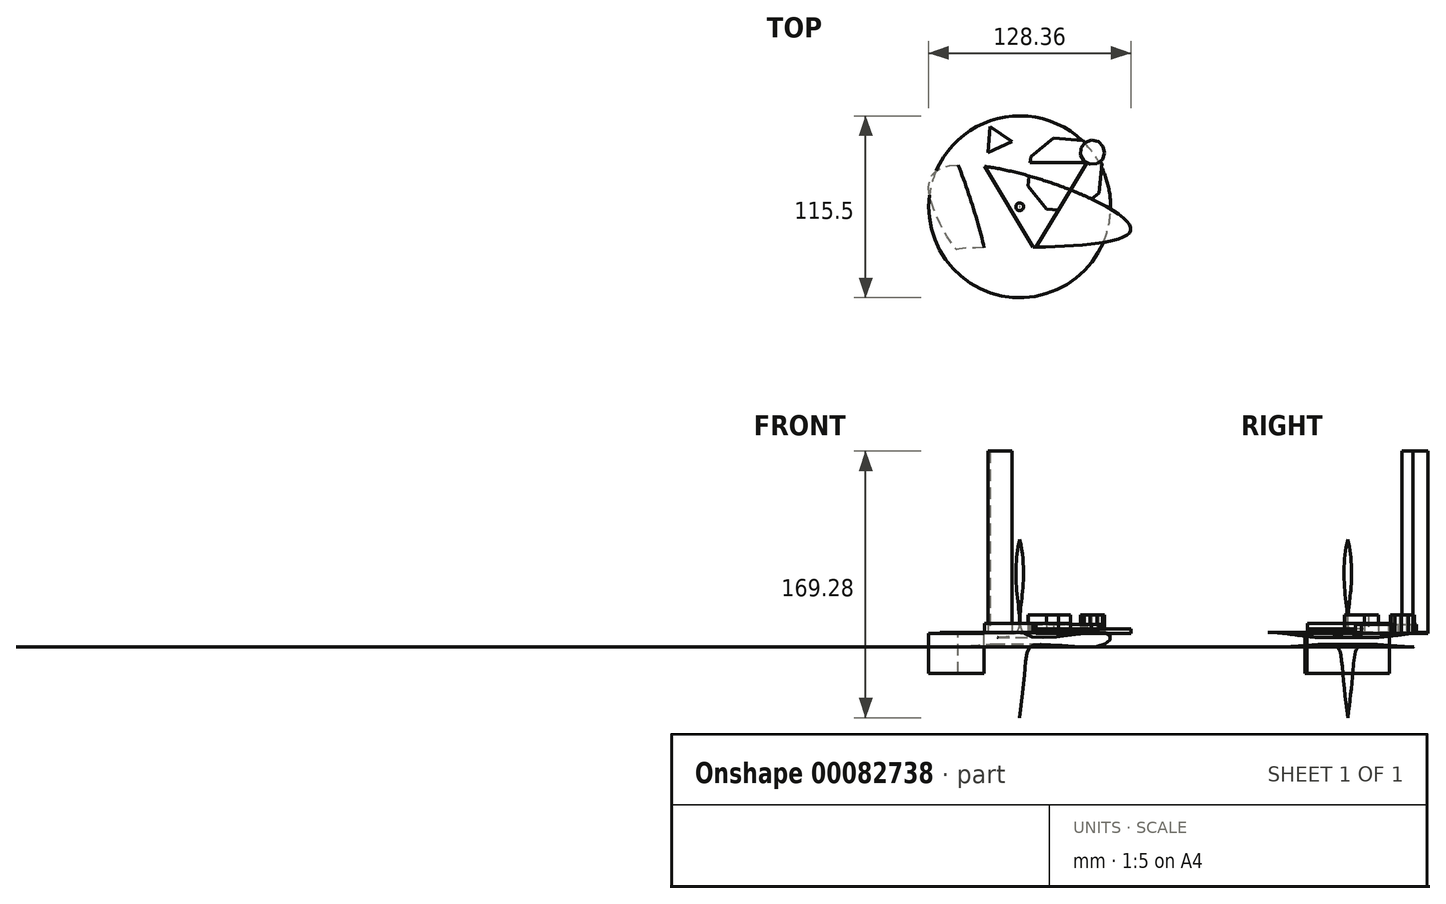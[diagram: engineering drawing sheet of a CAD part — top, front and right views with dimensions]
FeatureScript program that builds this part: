
annotation { "Feature Type Name" : "Feature", "Feature Type Description" : "" }
export const myFeature = defineFeature(function(context is Context, id is Id, definition is map)
    precondition{}
    {
        {
            var Q0;
            Q0=qCreatedBy(makeId("Top.planeOp"),FACE);
            var sketch = newSketch(context, id + "F0", { "sketchPlane" : qUnion([Q0])});
            skLineSegment(sketch, "E0", {"start": v(-23.89, 28.1) * mm, "end": v(42.66, 28.1) * mm});
            skLineSegment(sketch, "E1", {"start": v(42.66, 28.1) * mm, "end": v(9.39, -27.27) * mm});
            skPoint(sketch, "E1.endSnap0", {"position": v(9.39, 28.1) * mm});
            skLineSegment(sketch, "E2", {"start": v(9.39, -27.27) * mm, "end": v(-23.89, 28.1) * mm});
            skFitSpline(sketch, "E3", {"points": [v(-40.45, -27) * mm, v(-54.26, 21.88) * mm, v(70.55, -14.84) * mm, v(-38.66, -26.85) * mm, v(-40.45, -27) * mm]});
            skFitSpline(sketch, "E4", {"points": [v(-24.16, -51.02) * mm, v(-48.6, -46.6) * mm, v(-56.06, 54.05) * mm, v(-19.74, -40.25) * mm, v(-24.16, -51.02) * mm]});
            skCircle(sketch, "E5.cCircle", {"center": v(46.2, 34.64) * mm, "radius": 7.45 * mm, "construction": true});
            skLineSegment(sketch, "E5.0", {"start": v(44.59, 27.06) * mm, "end": v(40.74, 29.14) * mm});
            skLineSegment(sketch, "E5.1", {"start": v(40.74, 29.14) * mm, "end": v(38.63, 32.97) * mm});
            skLineSegment(sketch, "E5.2", {"start": v(38.63, 32.97) * mm, "end": v(38.93, 37.33) * mm});
            skLineSegment(sketch, "E5.3", {"start": v(38.93, 37.33) * mm, "end": v(41.54, 40.84) * mm});
            skLineSegment(sketch, "E5.4", {"start": v(41.54, 40.84) * mm, "end": v(45.63, 42.38) * mm});
            skLineSegment(sketch, "E5.5", {"start": v(45.63, 42.38) * mm, "end": v(49.9, 41.47) * mm});
            skLineSegment(sketch, "E5.6", {"start": v(49.9, 41.47) * mm, "end": v(53, 38.39) * mm});
            skLineSegment(sketch, "E5.7", {"start": v(53, 38.39) * mm, "end": v(53.95, 34.12) * mm});
            skLineSegment(sketch, "E5.8", {"start": v(53.95, 34.12) * mm, "end": v(52.44, 30.01) * mm});
            skLineSegment(sketch, "E5.9", {"start": v(52.44, 30.01) * mm, "end": v(48.95, 27.38) * mm});
            skLineSegment(sketch, "E5.10", {"start": v(48.95, 27.38) * mm, "end": v(44.59, 27.06) * mm});
            skPoint(sketch, "E5.0.midPoint", {"position": v(42.66, 28.1) * mm});
            skCircle(sketch, "E6.cCircle", {"center": v(28.68, 20.27) * mm, "radius": 22.67 * mm, "construction": true});
            skLineSegment(sketch, "E6.0", {"start": v(40.25, 41.9) * mm, "end": v(52.16, 27.39) * mm});
            skLineSegment(sketch, "E6.1", {"start": v(52.16, 27.39) * mm, "end": v(50.32, 8.7) * mm});
            skLineSegment(sketch, "E6.2", {"start": v(50.32, 8.7) * mm, "end": v(35.8, -3.21) * mm});
            skLineSegment(sketch, "E6.3", {"start": v(35.8, -3.21) * mm, "end": v(17.12, -1.37) * mm});
            skLineSegment(sketch, "E6.4", {"start": v(17.12, -1.37) * mm, "end": v(5.2, 13.15) * mm});
            skLineSegment(sketch, "E6.5", {"start": v(5.2, 13.15) * mm, "end": v(7.05, 31.83) * mm});
            skLineSegment(sketch, "E6.6", {"start": v(7.05, 31.83) * mm, "end": v(21.57, 43.74) * mm});
            skLineSegment(sketch, "E6.7", {"start": v(21.57, 43.74) * mm, "end": v(40.25, 41.9) * mm});
            skCircle(sketch, "E7.cCircle", {"center": v(-14.66, 42.23) * mm, "radius": 4.85 * mm, "construction": true});
            skLineSegment(sketch, "E7.0", {"start": v(-5, 41.39) * mm, "end": v(-20.22, 34.29) * mm});
            skLineSegment(sketch, "E7.1", {"start": v(-20.22, 34.29) * mm, "end": v(-18.76, 51.02) * mm});
            skLineSegment(sketch, "E7.2", {"start": v(-18.76, 51.02) * mm, "end": v(-5, 41.39) * mm});
            skPoint(sketch, "E7.0.midPoint", {"position": v(-12.61, 37.84) * mm});
            skSolve(sketch);
        }
        {
            var Q0;
            {var subQ0=sQuery(id+"F0.wireOp",EDGE,"E6.4");Q0=makeQuery(id+"F0.imprint","IMPRINT",FACE,{"disambiguationData":[TD([[makeQuery(id+"F0.imprint","IMPRINT",EDGE,{"derivedFrom":subQ0}),-1.0]])]});}
            var Q1;
            {var subQ8=sQuery(id+"F0.wireOp",EDGE,"E6.4");Q1=makeQuery(id+"F0.imprint","IMPRINT",FACE,{"disambiguationData":[TD([[makeQuery(id+"F0.imprint","IMPRINT",EDGE,{"derivedFrom":subQ8}),1.0]])]});}
            extrude(context, id + "F1", {"entities" : qUnion([Q0, Q1]), "depth" : 6.64 * mm});
        }
        {
            var Q0;
            {var subQ0=sQuery(id+"F0.wireOp",EDGE,"E4");var subQ1=sQuery(id+"F0.wireOp",EDGE,"E3");var subQ2=makeQuery(id+"F0.imprint","INTERSECT",VERTEX,{"disambiguationData":[OD(0.0)],"derivedFrom":[subQ1,subQ0]});Q0=makeQuery(id+"F0.imprint","IMPRINT",FACE,{"disambiguationData":[TD([[makeQuery(id+"F0.imprint","IMPRINT",EDGE,{"disambiguationData":[TD([[subQ2,1.0]])],"derivedFrom":subQ1}),-1.0]])]});}
            extrude(context, id + "F2", {"entities" : qUnion([Q0]), "oppositeDirection" : true, "depth" : 25.4 * mm});
        }
        {
            var Q0;
            {var subQ5=sQuery(id+"F0.wireOp",EDGE,"E5.1");Q0=makeQuery(id+"F0.imprint","IMPRINT",FACE,{"disambiguationData":[TD([[makeQuery(id+"F0.imprint","IMPRINT",EDGE,{"derivedFrom":subQ5}),1.0]])]});}
            var Q1;
            {var subQ0=sQuery(id+"F0.wireOp",EDGE,"E5.10");Q1=makeQuery(id+"F0.imprint","IMPRINT",FACE,{"disambiguationData":[TD([[makeQuery(id+"F0.imprint","IMPRINT",EDGE,{"derivedFrom":subQ0}),1.0]])]});}
            extrude(context, id + "F3", {"entities" : qUnion([Q0, Q1]), "depth" : 5.72 * mm});
        }
        {
            var Q0;
            {var subQ0=sQuery(id+"F0.wireOp",EDGE,"E6.4");Q0=makeQuery(id+"F0.imprint","IMPRINT",FACE,{"disambiguationData":[TD([[makeQuery(id+"F0.imprint","IMPRINT",EDGE,{"derivedFrom":subQ0}),-1.0]])]});}
            var Q1;
            {var subQ0=sQuery(id+"F0.wireOp",EDGE,"E5.4");Q1=makeQuery(id+"F0.imprint","IMPRINT",FACE,{"disambiguationData":[TD([[makeQuery(id+"F0.imprint","IMPRINT",EDGE,{"derivedFrom":subQ0}),-1.0]])]});}
            var Q2;
            {var subQ4=sQuery(id+"F0.wireOp",EDGE,"E5.1");Q2=makeQuery(id+"F0.imprint","IMPRINT",FACE,{"disambiguationData":[TD([[makeQuery(id+"F0.imprint","IMPRINT",EDGE,{"derivedFrom":subQ4}),-1.0]])]});}
            extrude(context, id + "F4", {"entities" : qUnion([Q0, Q1, Q2]), "depth" : 11.86 * mm});
        }
        {
            var Q0;
            {var subQ0=sQuery(id+"F0.wireOp",EDGE,"E3");var subQ1=sQuery(id+"F0.wireOp",EDGE,"E1");var subQ2=makeQuery(id+"F0.imprint","INTERSECT",VERTEX,{"disambiguationData":[OD(0.0)],"derivedFrom":[subQ1,subQ0]});Q0=makeQuery(id+"F0.imprint","IMPRINT",FACE,{"disambiguationData":[TD([[makeQuery(id+"F0.imprint","IMPRINT",EDGE,{"disambiguationData":[TD([[subQ2,1.0]])],"derivedFrom":subQ1}),1.0]])]});}
            var Q1;
            {var subQ0=sQuery(id+"F0.wireOp",EDGE,"E3");var subQ1=sQuery(id+"F0.wireOp",EDGE,"E1");var subQ2=makeQuery(id+"F0.imprint","INTERSECT",VERTEX,{"disambiguationData":[OD(1.0)],"derivedFrom":[subQ1,subQ0]});Q1=makeQuery(id+"F0.imprint","IMPRINT",FACE,{"disambiguationData":[TD([[makeQuery(id+"F0.imprint","IMPRINT",EDGE,{"disambiguationData":[TD([[subQ2,-1.0]])],"derivedFrom":subQ1}),1.0]])]});}
            extrude(context, id + "F5", {"entities" : qUnion([Q0, Q1]), "depth" : 2.93 * mm});
        }
        {
            var Q0;
            Q0=makeQuery(id+"F0.imprint","IMPRINT",FACE,{"disambiguationData":[TD([[makeQuery(id+"F0.imprint","IMPRINT",EDGE,{"derivedFrom":sQuery(id+"F0.wireOp",EDGE,"E7.0")}),-1.0]])]});
            extrude(context, id + "F6", {"entities" : qUnion([Q0]), "depth" : 115.92 * mm});
        }
        {
            var Q0;
            Q0=qCreatedBy(makeId("Front.planeOp"),FACE);
            var sketch = newSketch(context, id + "F7", { "sketchPlane" : qUnion([Q0])});
            skFitSpline(sketch, "E8", {"points": [v(0, 59.85) * mm, v(4.97, -1.17) * mm, v(56.33, 0) * mm, v(54.54, -6.42) * mm, v(12.15, -6.83) * mm, v(0, -53.36) * mm], "startDerivative": vector(93.6, -392.44) * mm, "endDerivative": vector(-76.35, -534.05) * mm});
            skLineSegment(sketch, "E9", {"start": v(0, 59.85) * mm, "end": v(0, -53.36) * mm});
            skLineSegment(sketch, "E10", {"start": v(0, 32.77) * mm, "end": v(0, 76.53) * mm});
            skPoint(sketch, "E11", {"position": v(0, 54.65) * mm});
            skSolve(sketch);
        }
        {
            var Q0;
            {var subQ0=sQuery(id+"F7.wireOp",EDGE,"E8");Q0=makeQuery(id+"F7.imprint","IMPRINT",FACE,{"disambiguationData":[TD([[makeQuery(id+"F7.imprint","IMPRINT",EDGE,{"derivedFrom":subQ0}),-1.0]])]});}
            var Q1;
            Q1=sQuery(id+"F7.wireOp",EDGE,"E10");
            revolve(context, id + "F8", {"entities" : qUnion([Q0]), "axis" : qUnion([Q1]), "revolveType" : RevolveType.FULL});
        }
    });
